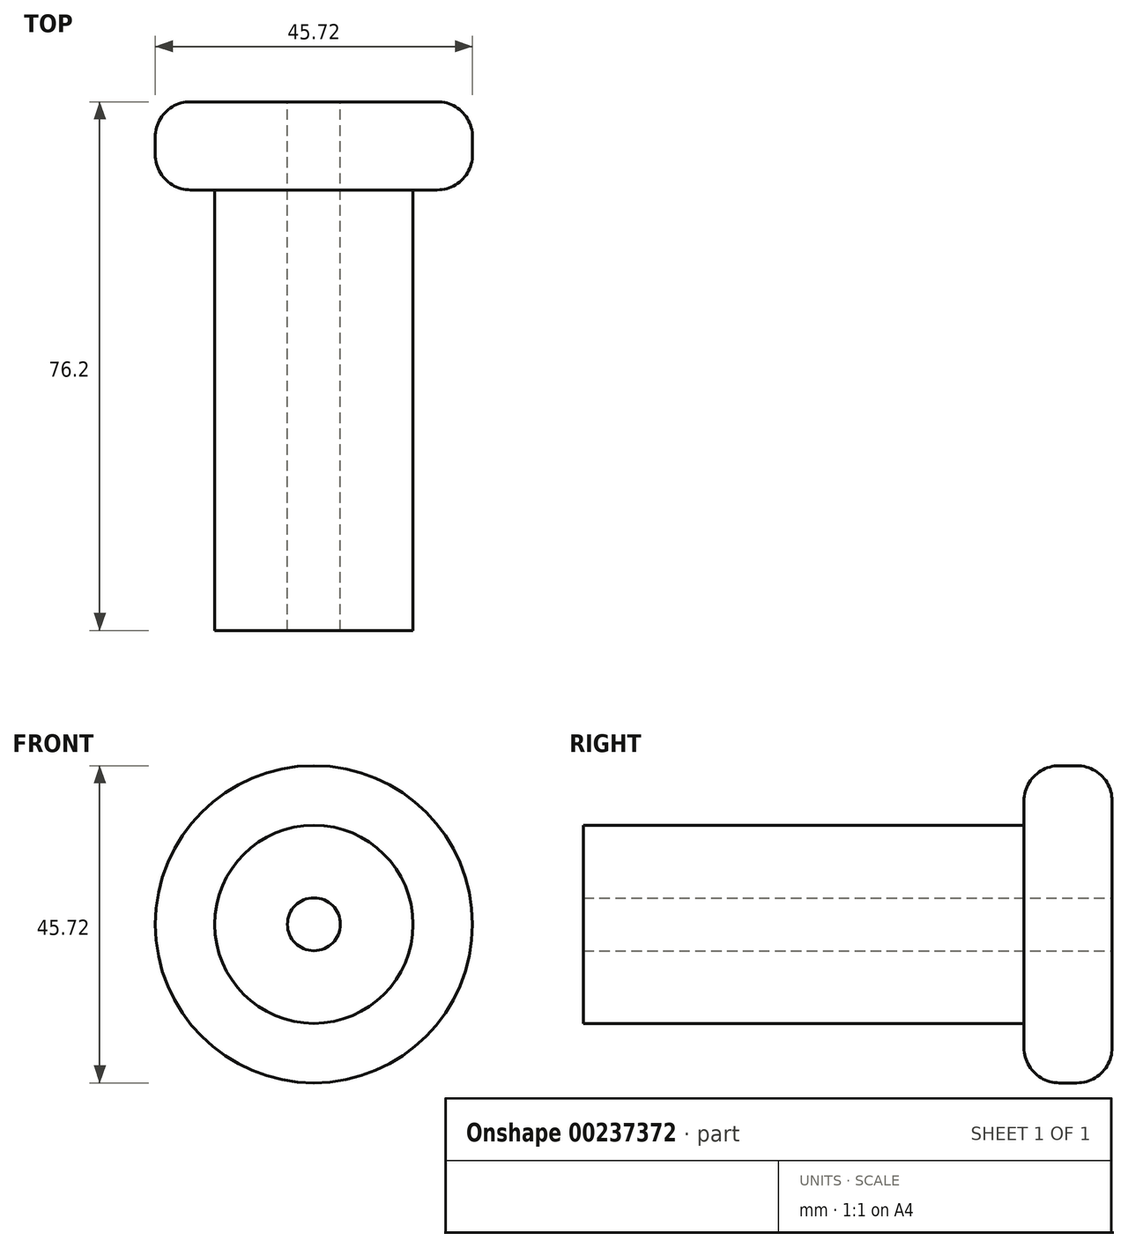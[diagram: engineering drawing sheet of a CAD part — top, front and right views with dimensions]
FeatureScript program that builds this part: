
annotation { "Feature Type Name" : "Feature", "Feature Type Description" : "" }
export const myFeature = defineFeature(function(context is Context, id is Id, definition is map)
    precondition{}
    {
        {
            var Q0;
            Q0=qCreatedBy(makeId("Front.planeOp"),FACE);
            var sketch = newSketch(context, id + "F0", { "sketchPlane" : qUnion([Q0])});
            skCircle(sketch, "E0", {"center": v(0, 0) * mm, "radius": 22.86 * mm});
            skCircle(sketch, "E1", {"center": v(0, 0) * mm, "radius": 14.29 * mm});
            skCircle(sketch, "E2", {"center": v(0, 0) * mm, "radius": 3.81 * mm});
            skSolve(sketch);
        }
        {
            var Q0;
            Q0=sQuery(id+"F0.wireOp",EDGE,"E1");
            extrude(context, id + "F1", {"bodyType" : ToolBodyType.SURFACE, "surfaceEntities" : qUnion([Q0]), "depth" : 76.2 * mm});
        }
        {
            var Q0;
            Q0 = qSketchRegion(id + "F0", true);
            extrude(context, id + "F2", {"entities" : qUnion([Q0]), "depth" : 12.7 * mm});
        }
        {
            var Q0;
            Q0=makeQuery(id+"F2.opExtrude","CAP_EDGE",EDGE,{"disambiguationData":[OSD([sQuery(id+"F0.wireOp",EDGE,"E0")])],"isStart":true});
            var Q1;
            Q1=makeQuery(id+"F2.opExtrude","CAP_EDGE",EDGE,{"disambiguationData":[OSD([sQuery(id+"F0.wireOp",EDGE,"E0")])],"isStart":false});
            fillet(context, id + "F3", {"entities" : qUnion([Q0, Q1]), "radius" : 5.08 * mm, "tangentPropagation" : true, "allowEdgeOverflow" : false});
        }
        {
            var Q0;
            Q0=sQuery(id+"F0.wireOp",EDGE,"E2");
            extrude(context, id + "F4", {"bodyType" : ToolBodyType.SURFACE, "surfaceEntities" : qUnion([Q0]), "depth" : 76.2 * mm});
        }
        {
            var Q0;
            Q0=makeQuery(id+"F0.imprint","IMPRINT",FACE,{"disambiguationData":[TD([[makeQuery(id+"F0.imprint","IMPRINT",EDGE,{"derivedFrom":sQuery(id+"F0.wireOp",EDGE,"E1")}),1.0]])]});
            extrude(context, id + "F5", {"entities" : qUnion([Q0]), "operationType" : NewBodyOperationType.ADD, "depth" : 76.2 * mm});
        }
    });
